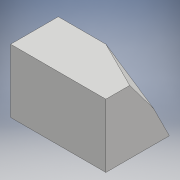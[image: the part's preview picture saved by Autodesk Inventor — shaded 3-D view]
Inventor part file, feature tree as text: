
AUTODESK INVENTOR PART (.ipt)
format: ipt  version: 2018 (Build 220112000, 112)  size: 139,264 bytes
history: native  units: mm
features: extrude x5, sketch x4, chamfer x2, other x2, loft x1
ambient origin geometry x8: Origin, YZ Plane, XZ Plane, XY Plane, X Axis, Y Axis, Z Axis, Center Point
bodies: Body1 (feature_tree)
feature tree (14):
  sketch  "Sketch3"  dims[d6=20.0mm d7=20.0mm d8=15.0mm d9=0.0mm]
  extrude  "Extrusion2"  Depth=20.0mm
  chamfer  "Chamfer3"  Distance=15.0mm
  extrude  "Extrusion3"  Depth=15.0mm TaperAngle=45.0deg
  extrude  "Extrusion5"  Depth=8.32mm TaperAngle=45.0deg
  chamfer  "Chamfer4"  Angle=180.0deg  [1 undecoded]
  sketch  "Sketch7"  dims[d28=5.0mm d29=0.0mm d30=8.32mm d31=5.0mm d32=45.0deg]
  extrude  "Extrusion6"  Depth=12.0mm
  extrude  "Extrusion7"  TaperAngle=90.0deg  [1 undecoded]
  loft  "Loft1"
  sketch  "Sketch6"  dims[d13=15.0mm d14=0.0mm d21=5.0mm d22=10.0mm d23=45.0deg]
  sketch  "Sketch8"  dims[d33=7.5mm d35=180.0deg d36=12.0mm d37=90.0deg d38=10.0mm d39=0.0mm d40=10.0mm d41=0.0mm d46=0.0mm d47=90.0deg d48=0.0mm d49=90.0deg]
  other  "Edges1"
  other  "Edges2"
note: 2 required parameter values undecoded (feature->parameter linkage not recoverable at this tier; creation-order binding heuristic only, values carry confidence <= 0.55)
